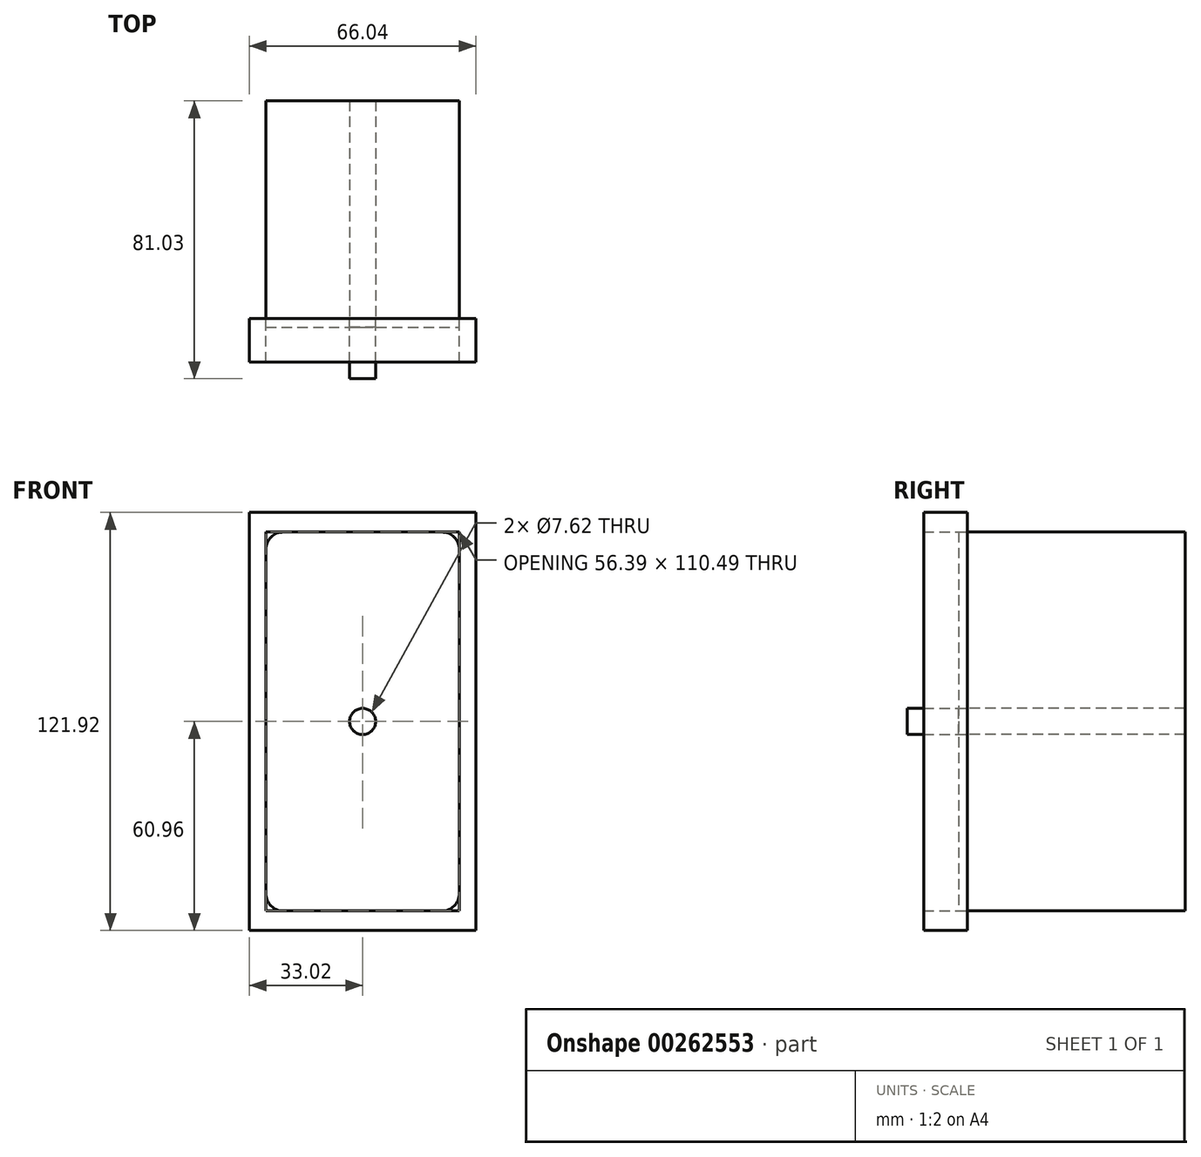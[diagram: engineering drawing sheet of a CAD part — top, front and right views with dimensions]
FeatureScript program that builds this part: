
annotation { "Feature Type Name" : "Feature", "Feature Type Description" : "" }
export const myFeature = defineFeature(function(context is Context, id is Id, definition is map)
    precondition{}
    {
        {
            var Q0;
            Q0=qCreatedBy(makeId("Front.planeOp"),FACE);
            var sketch = newSketch(context, id + "F0", { "sketchPlane" : qUnion([Q0])});
            skLineSegment(sketch, "E0.bottom", {"start": v(-33.02, 60.96) * mm, "end": v(33.02, 60.96) * mm});
            skLineSegment(sketch, "E0.top", {"start": v(-33.02, -60.96) * mm, "end": v(33.02, -60.96) * mm});
            skLineSegment(sketch, "E0.left", {"start": v(-33.02, 60.96) * mm, "end": v(-33.02, -60.96) * mm});
            skLineSegment(sketch, "E0.right", {"start": v(33.02, 60.96) * mm, "end": v(33.02, -60.96) * mm});
            skPoint(sketch, "E0.middle", {"position": v(0, 0) * mm});
            skLineSegment(sketch, "E1.bottom", {"start": v(-28.2, 55.24) * mm, "end": v(28.2, 55.24) * mm});
            skLineSegment(sketch, "E1.top", {"start": v(-28.2, -55.25) * mm, "end": v(28.2, -55.25) * mm});
            skLineSegment(sketch, "E1.left", {"start": v(-28.2, 55.24) * mm, "end": v(-28.2, -55.25) * mm});
            skLineSegment(sketch, "E1.right", {"start": v(28.2, 55.24) * mm, "end": v(28.2, -55.25) * mm});
            skCircle(sketch, "E2", {"center": v(0, 0) * mm, "radius": 3.81 * mm});
            skSolve(sketch);
        }
        {
            var Q0;
            Q0=makeQuery(id+"F0.imprint","IMPRINT",FACE,{"disambiguationData":[TD([[makeQuery(id+"F0.imprint","IMPRINT",EDGE,{"derivedFrom":sQuery(id+"F0.wireOp",EDGE,"E1.bottom")}),-1.0]])]});
            extrude(context, id + "F1", {"entities" : qUnion([Q0]), "depth" : 2.54 * mm});
        }
        {
            var Q0;
            Q0=makeQuery(id+"F0.imprint","IMPRINT",FACE,{"disambiguationData":[TD([[makeQuery(id+"F0.imprint","IMPRINT",EDGE,{"derivedFrom":sQuery(id+"F0.wireOp",EDGE,"E0.bottom")}),-1.0]])]});
            extrude(context, id + "F2", {"entities" : qUnion([Q0]), "depth" : 12.7 * mm});
        }
        {
            var Q0;
            Q0=makeQuery(id+"F2.opExtrude","SWEPT_EDGE",EDGE,{"disambiguationData":[OSD([sQuery(id+"F0.wireOp",EDGE,"E1.bottom"),sQuery(id+"F0.wireOp",EDGE,"E1.right")])]});
            var Q1;
            Q1=makeQuery(id+"F2.opExtrude","SWEPT_EDGE",EDGE,{"disambiguationData":[OSD([sQuery(id+"F0.wireOp",EDGE,"E1.bottom"),sQuery(id+"F0.wireOp",EDGE,"E1.left")])]});
            var Q2;
            Q2=makeQuery(id+"F2.opExtrude","SWEPT_EDGE",EDGE,{"disambiguationData":[OSD([sQuery(id+"F0.wireOp",EDGE,"E1.top"),sQuery(id+"F0.wireOp",EDGE,"E1.right")])]});
            var Q3;
            Q3=makeQuery(id+"F2.opExtrude","SWEPT_EDGE",EDGE,{"disambiguationData":[OSD([sQuery(id+"F0.wireOp",EDGE,"E1.top"),sQuery(id+"F0.wireOp",EDGE,"E1.left")])]});
            fillet(context, id + "F3", {"entities" : qUnion([Q0, Q1, Q2, Q3]), "radius" : 5.08 * mm, "tangentPropagation" : true, "allowEdgeOverflow" : false});
        }
        {
            var Q0;
            Q0=makeQuery(id+"F1.opExtrude","CAP_FACE",FACE,{"disambiguationData":[OSD([sQuery(id+"F0.wireOp",EDGE,"E1.bottom"),sQuery(id+"F0.wireOp",EDGE,"E1.top"),sQuery(id+"F0.wireOp",EDGE,"E1.left"),sQuery(id+"F0.wireOp",EDGE,"E1.right")])],"isStart":true});
            extrude(context, id + "F4", {"entities" : qUnion([Q0]), "depth" : 63.5 * mm});
        }
        {
            var Q0;
            Q0=makeQuery(id+"F0.imprint","IMPRINT",FACE,{"disambiguationData":[TD([[makeQuery(id+"F0.imprint","IMPRINT",EDGE,{"derivedFrom":sQuery(id+"F0.wireOp",EDGE,"E2")}),1.0]])]});
            extrude(context, id + "F5", {"entities" : qUnion([Q0]), "depth" : 17.53 * mm});
        }
    });
